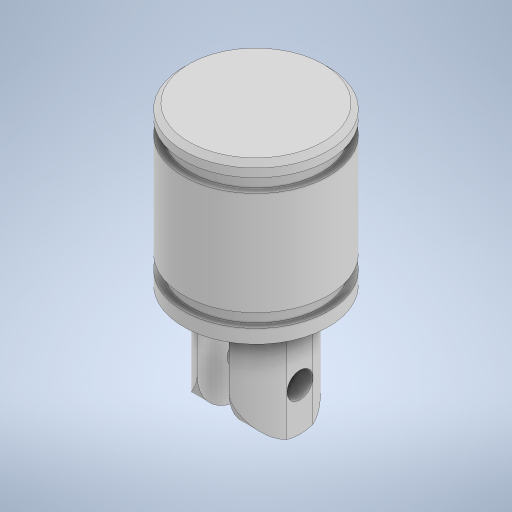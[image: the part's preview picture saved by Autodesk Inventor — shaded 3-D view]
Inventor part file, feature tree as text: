
AUTODESK INVENTOR PART (.ipt)
format: ipt  version: 2023 (Build 270158000, 158)  size: 334,848 bytes
history: native  units: in
note: dims shown in document units (in); Inventor stores cm internally (conversion verified against a paired STEP export)
features: sketch x3, extrude x2, revolve x1, chamfer x1, fillet x1
ambient origin geometry x8: Origin, YZ Plane, XZ Plane, XY Plane, X Axis, Y Axis, Z Axis, Center Point
bodies: Solid1 (feature_tree)
feature tree (8):
  revolve  "Revolution1"  [1 undecoded]
  extrude  "Extrusion2"  Depth=0.132in
  chamfer  "Chamfer1"  Distance=1.0in
  fillet  "Fillet1"  Radius=0.066in
  extrude  "Extrusion3"  Depth=0.125in
  sketch  "Sketch1"  dims[d0=0.7017in d1=0.132in]
  sketch  "Sketch2"  dims[d2=0.066in d3=0.132in]
  sketch  "Sketch3"  dims[d4=0.066in d5=1.0in d6=0.066in d7=0.132in d8=0.066in d9=0.132in d10=90.0deg d18=0.125in d19=1.25in d20=0.0in d21=0.05in d22=0.125in d23=45.0deg d24=0.125in d25=1.25in d26=0.0in]
note: 1 required parameter value undecoded (feature->parameter linkage not recoverable at this tier; creation-order binding heuristic only, values carry confidence <= 0.55)
